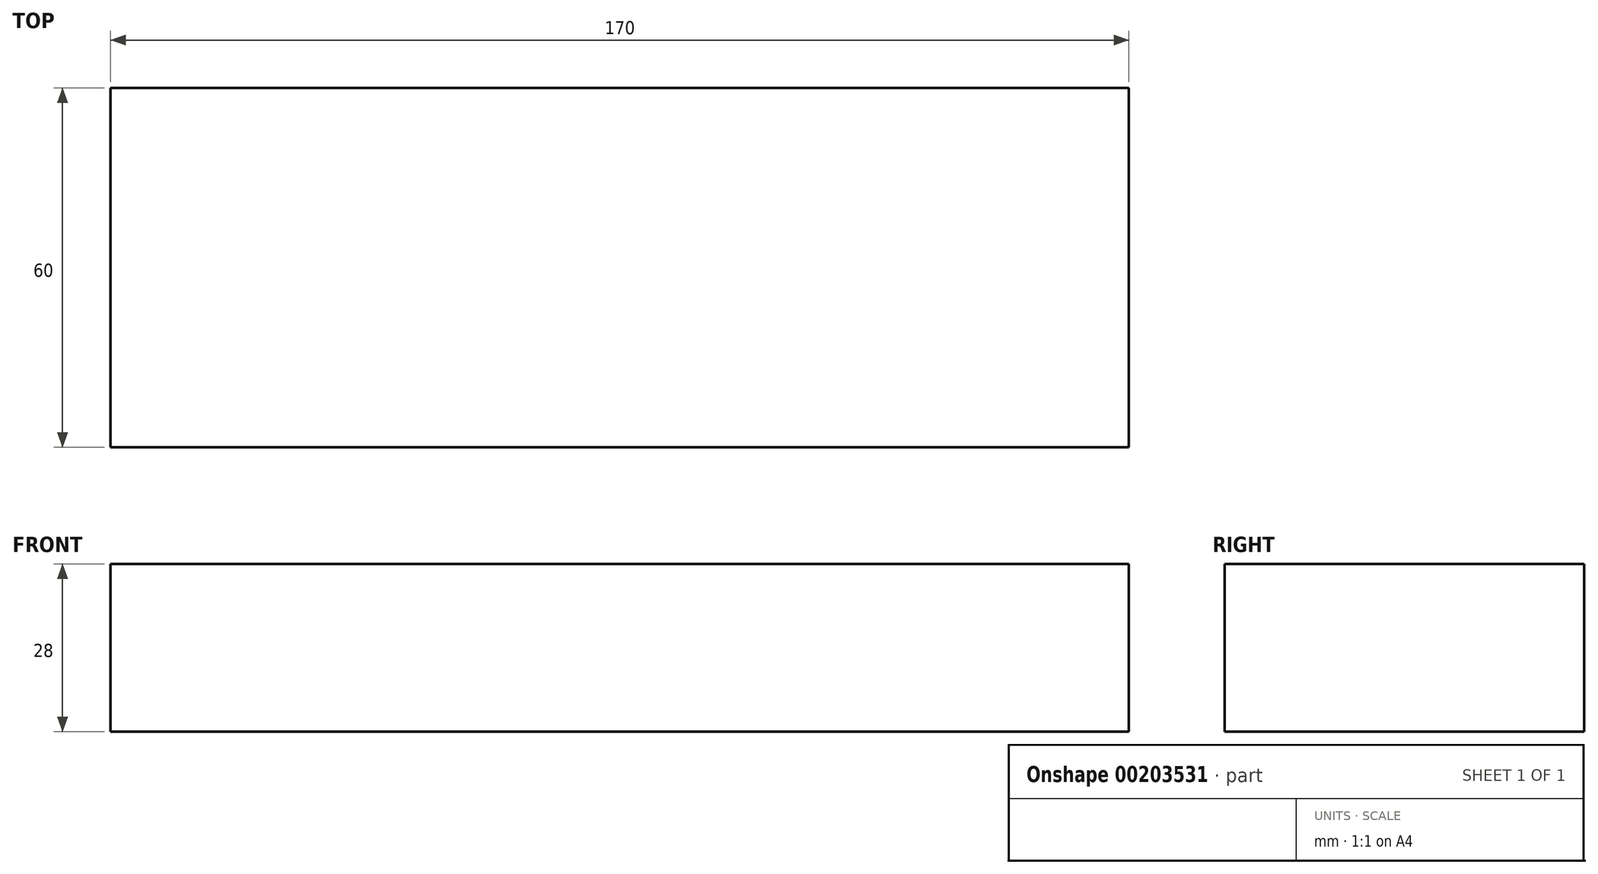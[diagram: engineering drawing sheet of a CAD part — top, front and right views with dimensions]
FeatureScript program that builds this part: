
annotation { "Feature Type Name" : "Feature", "Feature Type Description" : "" }
export const myFeature = defineFeature(function(context is Context, id is Id, definition is map)
    precondition{}
    {
        {
            var Q0;
            Q0=qCreatedBy(makeId("Top.planeOp"),FACE);
            var sketch = newSketch(context, id + "F0", { "sketchPlane" : qUnion([Q0])});
            skLineSegment(sketch, "E0.bottom", {"start": v(-85, 30) * mm, "end": v(85, 30) * mm});
            skLineSegment(sketch, "E0.top", {"start": v(-85, -30) * mm, "end": v(85, -30) * mm});
            skLineSegment(sketch, "E0.left", {"start": v(-85, 30) * mm, "end": v(-85, -30) * mm});
            skLineSegment(sketch, "E0.right", {"start": v(85, 30) * mm, "end": v(85, -30) * mm});
            skPoint(sketch, "E0.middle", {"position": v(0, 0) * mm});
            skSolve(sketch);
        }
        {
            var Q0;
            Q0=makeQuery(id+"F0.imprint","IMPRINT",FACE,{"disambiguationData":[TD([[makeQuery(id+"F0.imprint","IMPRINT",EDGE,{"derivedFrom":sQuery(id+"F0.wireOp",EDGE,"E0.bottom")}),-1.0]])]});
            extrude(context, id + "F1", {"entities" : qUnion([Q0]), "depth" : 28 * mm});
        }
    });
